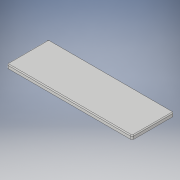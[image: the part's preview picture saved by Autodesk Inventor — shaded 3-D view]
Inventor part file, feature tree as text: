
AUTODESK INVENTOR PART (.ipt)
format: ipt  version: 2017 (Build 210142000, 142)  size: 110,592 bytes
history: native  units: in
note: dims shown in document units (in); Inventor stores cm internally (conversion verified against a paired STEP export)
features: extrude x1, fillet x1, sketch x1
ambient origin geometry x8: Origin, YZ Plane, XZ Plane, XY Plane, X Axis, Y Axis, Z Axis, Center Point
bodies: Solid1 (feature_tree)
feature tree (3):
  extrude  "main key board"  Depth=0.4792in
  fillet  "Fillet1"  Radius=1.4583in
  sketch  "Sketch1"  dims[d4=0.0417in d5=0.4792in d6=1.4583in d7=0.0417in d8=0.0in d9=0.01in]
